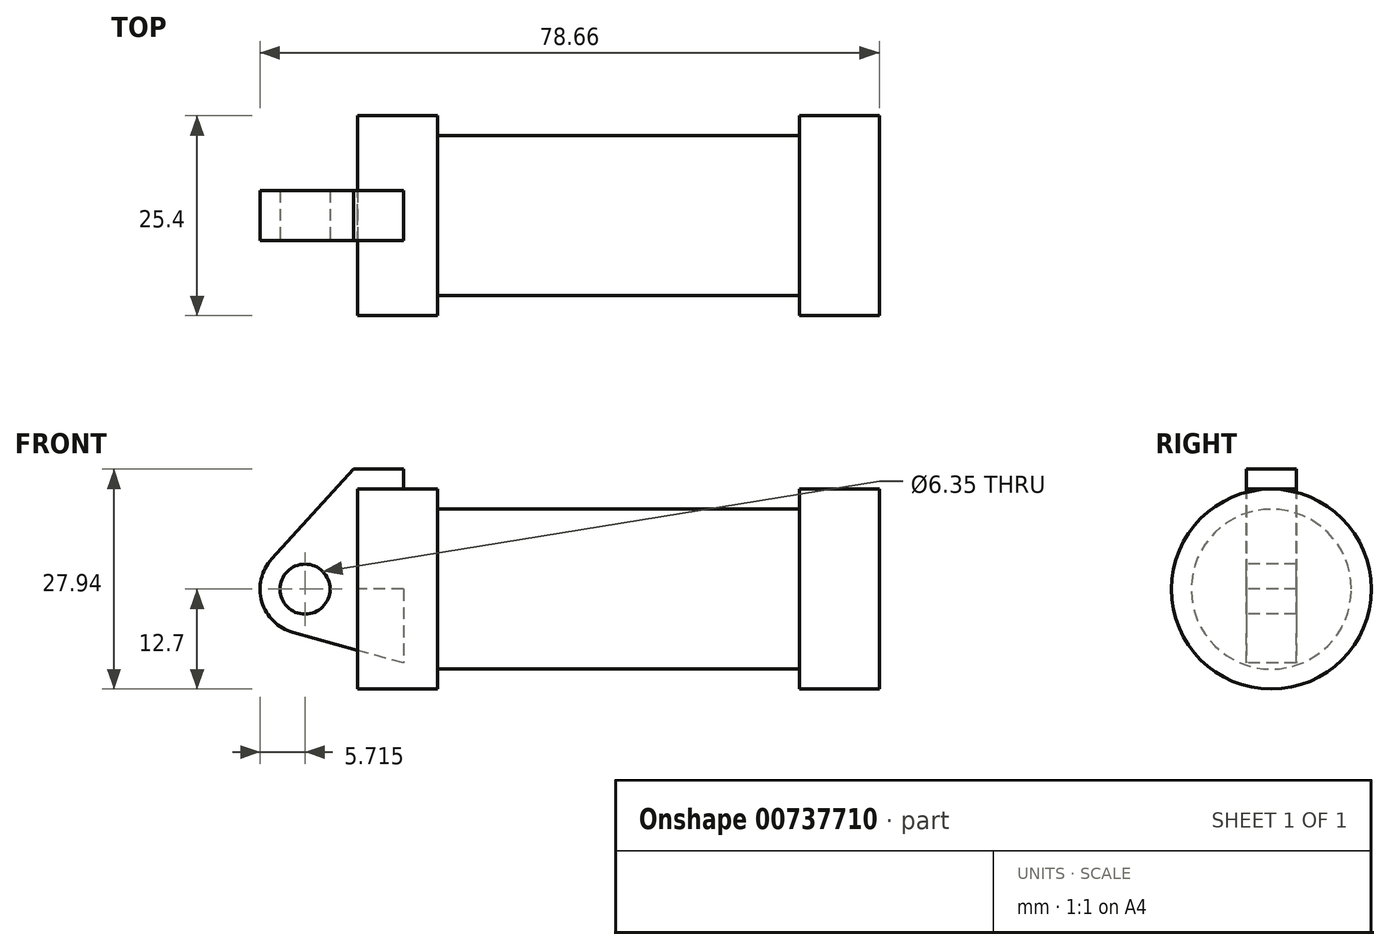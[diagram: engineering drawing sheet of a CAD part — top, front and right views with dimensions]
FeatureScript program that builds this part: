
annotation { "Feature Type Name" : "Feature", "Feature Type Description" : "" }
export const myFeature = defineFeature(function(context is Context, id is Id, definition is map)
    precondition{}
    {
        {
            var Q0;
            Q0=qCreatedBy(makeId("Front.planeOp"),FACE);
            var sketch = newSketch(context, id + "F0", { "sketchPlane" : qUnion([Q0])});
            skLineSegment(sketch, "E0", {"start": v(0, 0) * mm, "end": v(0, 12.7) * mm});
            skLineSegment(sketch, "E1", {"start": v(0, 12.7) * mm, "end": v(10.16, 12.7) * mm});
            skLineSegment(sketch, "E2", {"start": v(10.16, 12.7) * mm, "end": v(10.16, 10.16) * mm});
            skLineSegment(sketch, "E3", {"start": v(10.16, 10.16) * mm, "end": v(56.13, 10.16) * mm});
            skLineSegment(sketch, "E4", {"start": v(56.13, 10.16) * mm, "end": v(56.13, 12.7) * mm});
            skLineSegment(sketch, "E5", {"start": v(56.13, 12.7) * mm, "end": v(66.3, 12.7) * mm});
            skLineSegment(sketch, "E6", {"start": v(66.3, 12.7) * mm, "end": v(66.3, 0) * mm});
            skLineSegment(sketch, "E7", {"start": v(66.3, 0) * mm, "end": v(0, 0) * mm});
            skLineSegment(sketch, "E8", {"start": v(5.84, 15.24) * mm, "end": v(-0.5, 15.24) * mm});
            skLineSegment(sketch, "E9", {"start": v(-0.5, 15.24) * mm, "end": v(-10.88, 3.85) * mm});
            skLineSegment(sketch, "E10", {"start": v(0, 0) * mm, "end": v(-6.65, 0) * mm});
            skCircle(sketch, "E11", {"center": v(-6.65, 0) * mm, "radius": 5.72 * mm});
            skCircle(sketch, "E12", {"center": v(-6.65, 0) * mm, "radius": 3.18 * mm});
            skLineSegment(sketch, "E13", {"start": v(5.84, 15.24) * mm, "end": v(5.84, -9.4) * mm});
            skLineSegment(sketch, "E14", {"start": v(5.84, -9.4) * mm, "end": v(-8.18, -5.5) * mm});
            skSolve(sketch);
        }
        {
            var Q0;
            {var subQ0=sQuery(id+"F0.wireOp",EDGE,"E2");Q0=makeQuery(id+"F0.imprint","IMPRINT",FACE,{"disambiguationData":[TD([[makeQuery(id+"F0.imprint","IMPRINT",EDGE,{"derivedFrom":subQ0}),-1.0]])]});}
            var Q1;
            {var subQ0=sQuery(id+"F0.wireOp",EDGE,"E0");Q1=makeQuery(id+"F0.imprint","IMPRINT",FACE,{"disambiguationData":[TD([[makeQuery(id+"F0.imprint","IMPRINT",EDGE,{"derivedFrom":subQ0}),-1.0]])]});}
            var Q2;
            Q2=sQuery(id+"F0.wireOp",EDGE,"E7");
            revolve(context, id + "F1", {"surfaceOperationType" : NewSurfaceOperationType.NEW, "entities" : qUnion([Q0, Q1]), "axis" : qUnion([Q2]), "revolveType" : RevolveType.FULL});
        }
        {
            var Q0;
            {var subQ0=sQuery(id+"F0.wireOp",EDGE,"E14");Q0=makeQuery(id+"F0.imprint","IMPRINT",FACE,{"disambiguationData":[TD([[makeQuery(id+"F0.imprint","IMPRINT",EDGE,{"derivedFrom":subQ0}),-1.0]])]});}
            var Q1;
            {var subQ1=sQuery(id+"F0.wireOp",EDGE,"E0");Q1=makeQuery(id+"F0.imprint","IMPRINT",FACE,{"disambiguationData":[TD([[makeQuery(id+"F0.imprint","IMPRINT",EDGE,{"derivedFrom":subQ1}),1.0]])]});}
            var Q2;
            {var subQ5=sQuery(id+"F0.wireOp",EDGE,"E12");Q2=makeQuery(id+"F0.imprint","IMPRINT",FACE,{"disambiguationData":[TD([[makeQuery(id+"F0.imprint","IMPRINT",EDGE,{"derivedFrom":subQ5}),-1.0]])]});}
            extrude(context, id + "F2", {"entities" : qUnion([Q0, Q1, Q2]), "endBound" : BoundingType.SYMMETRIC, "oppositeDirection" : true, "depth" : 6.35 * mm, "offsetDistance" : 25.4 * mm});
        }
    });
